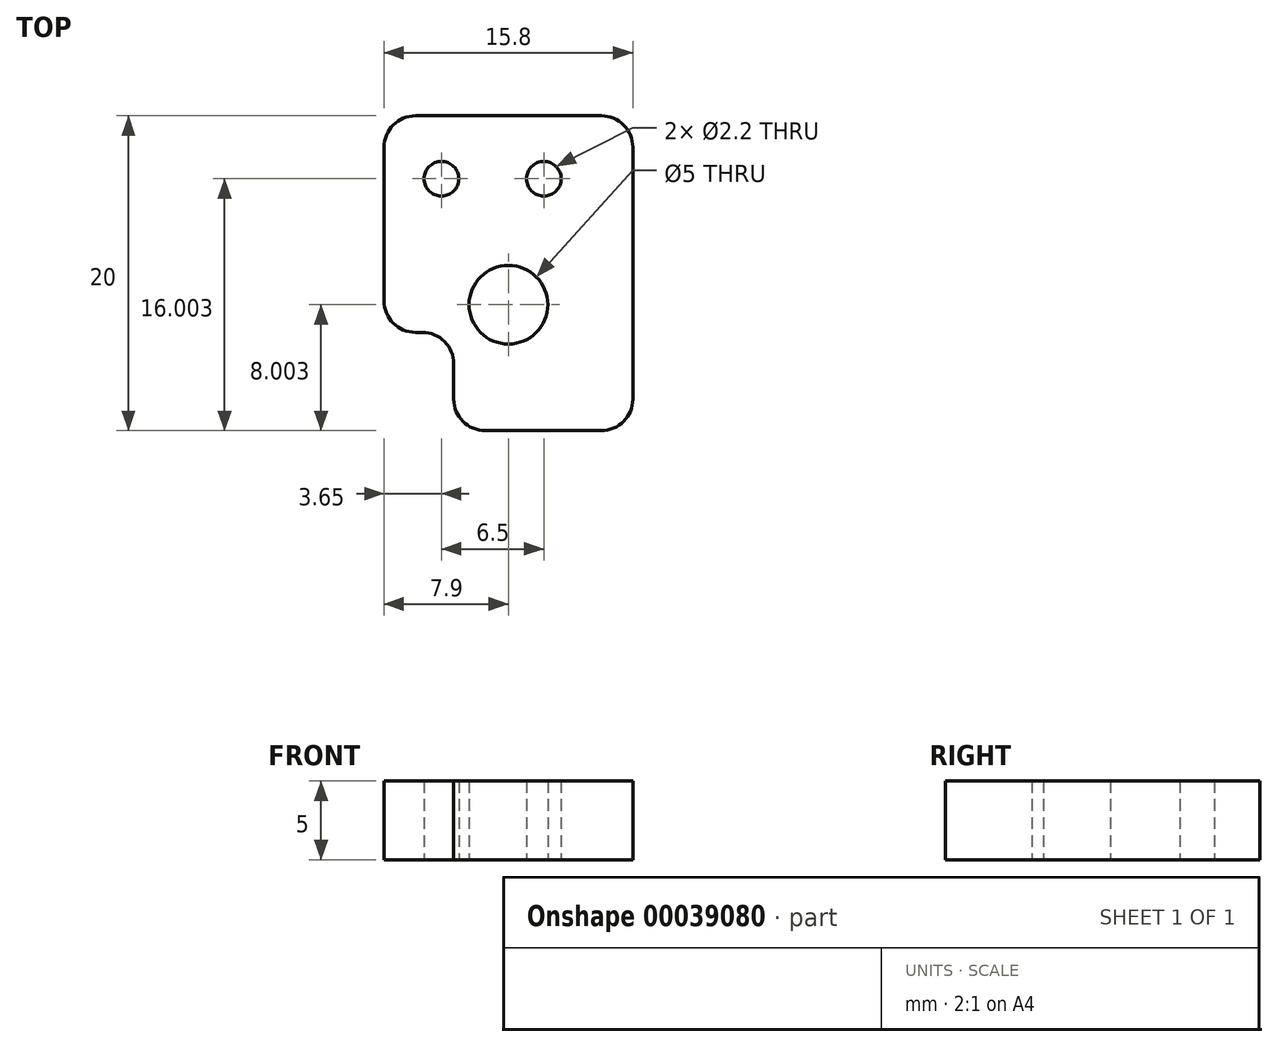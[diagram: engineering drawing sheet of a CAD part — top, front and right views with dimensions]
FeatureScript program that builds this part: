
annotation { "Feature Type Name" : "Feature", "Feature Type Description" : "" }
export const myFeature = defineFeature(function(context is Context, id is Id, definition is map)
    precondition{}
    {
        {
            var Q0;
            Q0=qCreatedBy(makeId("Top.planeOp"),FACE);
            var sketch = newSketch(context, id + "F0", { "sketchPlane" : qUnion([Q0])});
            skLineSegment(sketch, "E0.bottom", {"start": v(0, 23.83) * mm, "end": v(0, 23.83) * mm});
            skLineSegment(sketch, "E0.top", {"start": v(0, -23.13) * mm, "end": v(0, -23.13) * mm});
            skLineSegment(sketch, "E0.left", {"start": v(0, 23.83) * mm, "end": v(0, -23.13) * mm, "construction": true});
            skLineSegment(sketch, "E0.right", {"start": v(0, 23.83) * mm, "end": v(0, -23.13) * mm, "construction": true});
            skLineSegment(sketch, "E1", {"start": v(0, 8.4) * mm, "end": v(-7.9, 8.4) * mm});
            skLineSegment(sketch, "E2", {"start": v(-7.9, 8.4) * mm, "end": v(-7.9, -11.6) * mm});
            skLineSegment(sketch, "E3", {"start": v(-7.9, -11.6) * mm, "end": v(0, -11.6) * mm});
            skLineSegment(sketch, "E4.MirrorCS", {"start": v(0, 8.4) * mm, "end": v(7.9, 8.4) * mm});
            skLineSegment(sketch, "E5.MirrorCS", {"start": v(7.9, 8.4) * mm, "end": v(7.9, -11.6) * mm});
            skLineSegment(sketch, "E6.MirrorCS", {"start": v(7.9, -11.6) * mm, "end": v(0, -11.6) * mm});
            skCircle(sketch, "E7", {"center": v(0, -3.6) * mm, "radius": 2.5 * mm});
            skCircle(sketch, "E8", {"center": v(-4.25, 4.4) * mm, "radius": 1.1 * mm});
            skCircle(sketch, "E9.MirrorC", {"center": v(2.25, 4.4) * mm, "radius": 1.1 * mm});
            skLineSegment(sketch, "E10.bottom", {"start": v(-7.9, -11.6) * mm, "end": v(-3.47, -11.6) * mm});
            skLineSegment(sketch, "E10.top", {"start": v(-7.9, -5.37) * mm, "end": v(-3.47, -5.37) * mm});
            skLineSegment(sketch, "E10.left", {"start": v(-7.9, -11.6) * mm, "end": v(-7.9, -5.37) * mm});
            skLineSegment(sketch, "E10.right", {"start": v(-3.47, -11.6) * mm, "end": v(-3.47, -5.37) * mm});
            skSolve(sketch);
        }
        {
            var Q0;
            Q0=makeQuery(id+"F0.imprint","IMPRINT",FACE,{"disambiguationData":[TD([[makeQuery(id+"F0.imprint","IMPRINT",EDGE,{"derivedFrom":sQuery(id+"F0.wireOp",EDGE,"E1")}),1.0]])]});
            extrude(context, id + "F1", {"entities" : qUnion([Q0]), "depth" : 5 * mm});
        }
        {
            var Q0;
            Q0=makeQuery(id+"F1.opExtrude","SWEPT_EDGE",EDGE,{"disambiguationData":[OSD([sQuery(id+"F0.wireOp",EDGE,"E5.MirrorCS"),sQuery(id+"F0.wireOp",EDGE,"E6.MirrorCS")])]});
            var Q1;
            Q1=makeQuery(id+"F1.opExtrude","SWEPT_EDGE",EDGE,{"disambiguationData":[OSD([sQuery(id+"F0.wireOp",EDGE,"E4.MirrorCS"),sQuery(id+"F0.wireOp",EDGE,"E5.MirrorCS")])]});
            var Q2;
            Q2=makeQuery(id+"F1.opExtrude","SWEPT_EDGE",EDGE,{"disambiguationData":[OSD([sQuery(id+"F0.wireOp",EDGE,"E2"),sQuery(id+"F0.wireOp",EDGE,"E3")])]});
            var Q3;
            Q3=makeQuery(id+"F1.opExtrude","SWEPT_EDGE",EDGE,{"disambiguationData":[OSD([sQuery(id+"F0.wireOp",EDGE,"E1"),sQuery(id+"F0.wireOp",EDGE,"E2")])]});
            var Q4;
            Q4=makeQuery(id+"F1.opExtrude","SWEPT_EDGE",EDGE,{"disambiguationData":[OSD([sQuery(id+"F0.wireOp",EDGE,"E2"),sQuery(id+"F0.wireOp",EDGE,"E10.top"),sQuery(id+"F0.wireOp",EDGE,"E10.left")])]});
            var Q5;
            Q5=makeQuery(id+"F1.opExtrude","SWEPT_EDGE",EDGE,{"disambiguationData":[OSD([sQuery(id+"F0.wireOp",EDGE,"E10.top"),sQuery(id+"F0.wireOp",EDGE,"E10.right")])]});
            var Q6;
            Q6=makeQuery(id+"F1.opExtrude","SWEPT_EDGE",EDGE,{"disambiguationData":[OSD([sQuery(id+"F0.wireOp",EDGE,"E3"),sQuery(id+"F0.wireOp",EDGE,"E10.bottom"),sQuery(id+"F0.wireOp",EDGE,"E10.right")])]});
            fillet(context, id + "F2", {"entities" : qUnion([Q0, Q1, Q2, Q3, Q4, Q5, Q6]), "radius" : 2 * mm, "tangentPropagation" : true, "allowEdgeOverflow" : false});
        }
    });
